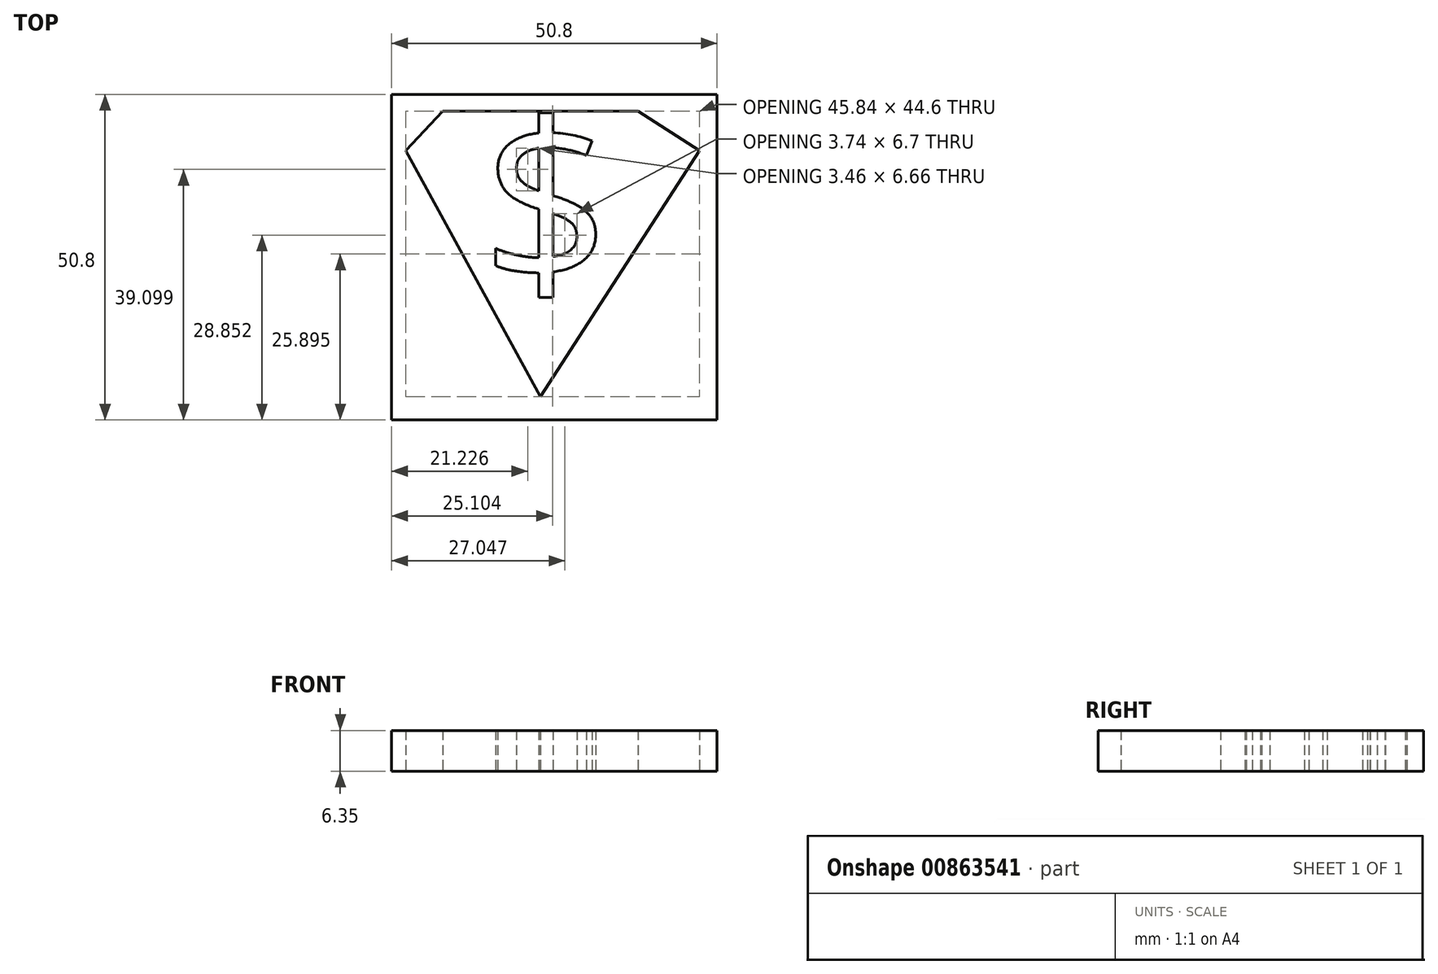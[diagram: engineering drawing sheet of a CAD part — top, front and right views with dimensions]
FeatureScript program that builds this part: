
annotation { "Feature Type Name" : "Feature", "Feature Type Description" : "" }
export const myFeature = defineFeature(function(context is Context, id is Id, definition is map)
    precondition{}
    {
        {
            var Q0;
            Q0=qCreatedBy(makeId("Top.planeOp"),FACE);
            var sketch = newSketch(context, id + "F0", { "sketchPlane" : qUnion([Q0])});
            skLineSegment(sketch, "E0.bottom", {"start": v(0, 0) * mm, "end": v(50.8, 0) * mm});
            skLineSegment(sketch, "E0.top", {"start": v(0, 50.8) * mm, "end": v(50.8, 50.8) * mm});
            skLineSegment(sketch, "E0.left", {"start": v(0, 0) * mm, "end": v(0, 50.8) * mm});
            skLineSegment(sketch, "E0.right", {"start": v(50.8, 0) * mm, "end": v(50.8, 50.8) * mm});
            skLineSegment(sketch, "E1", {"start": v(8, 48.2) * mm, "end": v(38.44, 48.2) * mm});
            skLineSegment(sketch, "E2", {"start": v(38.44, 48.2) * mm, "end": v(48.02, 42.03) * mm});
            skLineSegment(sketch, "E3", {"start": v(48.02, 42.03) * mm, "end": v(23.22, 3.6) * mm});
            skPoint(sketch, "E3.endSnap0", {"position": v(23.22, 48.2) * mm});
            skLineSegment(sketch, "E4", {"start": v(23.22, 3.6) * mm, "end": v(2.19, 42.03) * mm});
            skLineSegment(sketch, "E5", {"start": v(2.19, 42.03) * mm, "end": v(8, 48.2) * mm});
            skText(sketch, "E6", { "text": "$\n", "fontName": "OpenSans-Regular.ttf"});
            const initialGuessF0  = {"E6": [0.014, 0.02116, 1, 0, 0.0254]};
            skSetInitialGuess(sketch, initialGuessF0);
            skSolve(sketch);
        }
        {
            var Q0;
            Q0=makeQuery(id+"F0.imprint","IMPRINT",FACE,{"disambiguationData":[TD([[makeQuery(id+"F0.imprint","IMPRINT",EDGE,{"derivedFrom":sQuery(id+"F0.wireOp",EDGE,"E0.bottom")}),1.0]])]});
            var Q1;
            Q1=makeQuery(id+"F0.imprint","IMPRINT",FACE,{"disambiguationData":[TD([[makeQuery(id+"F0.imprint","IMPRINT",EDGE,{"derivedFrom":sQuery(id+"F0.wireOp",EDGE,"E6.sketch_text.stroke-0")}),-1.0]])]});
            extrude(context, id + "F1", {"entities" : qUnion([Q0, Q1]), "depth" : 6.35 * mm, "offsetDistance" : 25.4 * mm});
        }
    });
